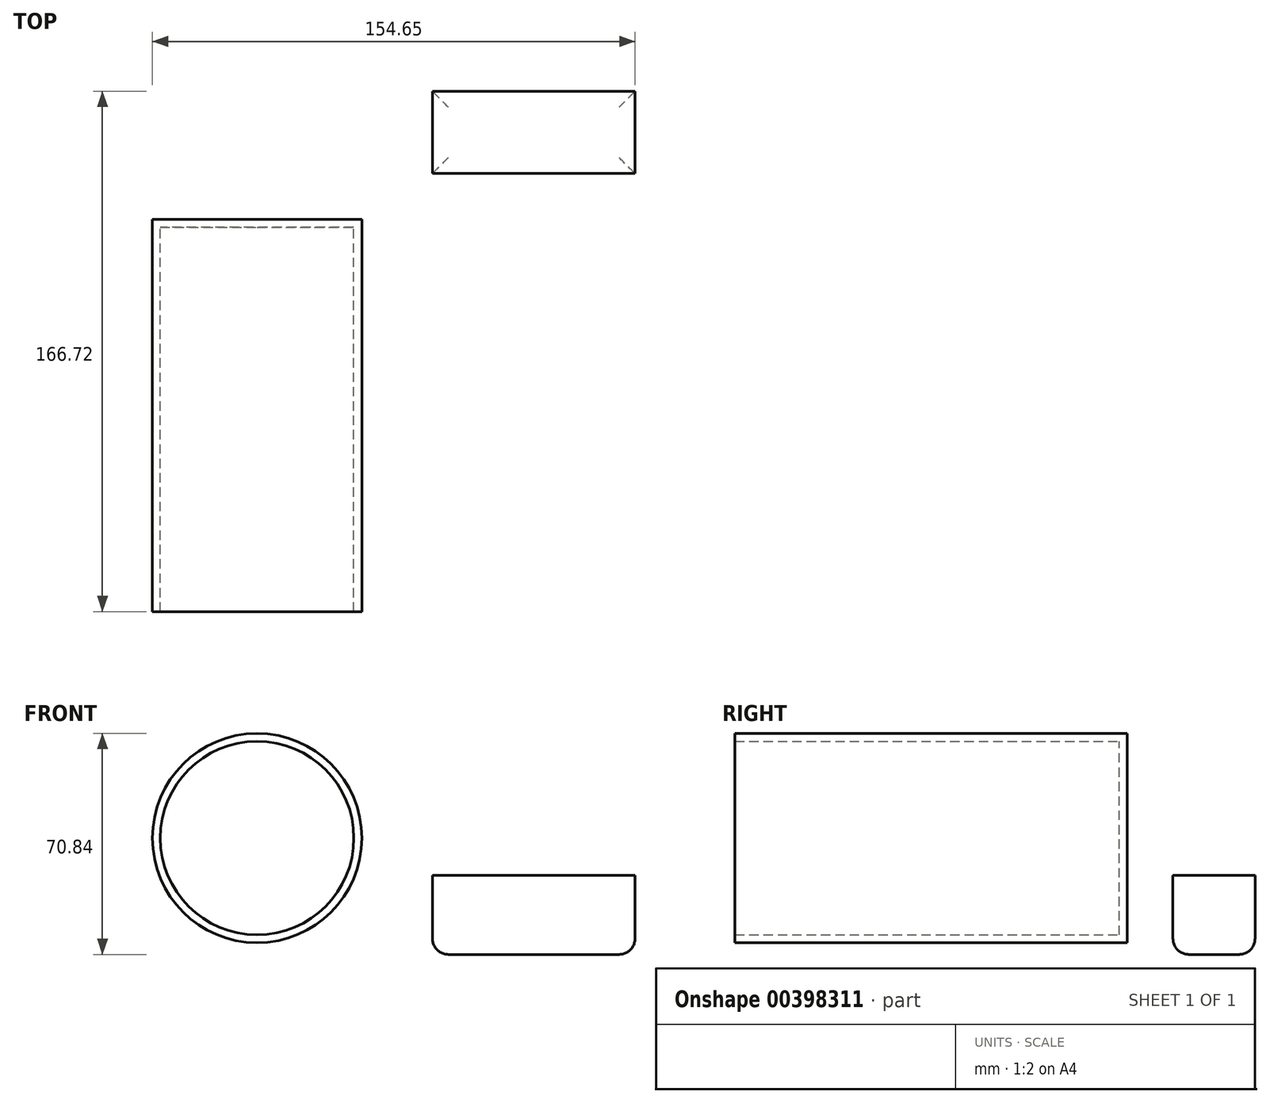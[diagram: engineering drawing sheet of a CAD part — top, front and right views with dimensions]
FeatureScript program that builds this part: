
annotation { "Feature Type Name" : "Feature", "Feature Type Description" : "" }
export const myFeature = defineFeature(function(context is Context, id is Id, definition is map)
    precondition{}
    {
        {
            var Q0;
            Q0=qCreatedBy(makeId("Front.planeOp"),FACE);
            var sketch = newSketch(context, id + "F0", { "sketchPlane" : qUnion([Q0])});
            skCircle(sketch, "E0", {"center": v(-48.38, 37.3) * mm, "radius": 33.55 * mm});
            skSolve(sketch);
        }
        {
            var Q0;
            Q0 = qSketchRegion(id + "F0", true);
            extrude(context, id + "F1", {"entities" : qUnion([Q0]), "depth" : 125.73 * mm});
        }
        {
            var Q0;
            Q0=makeQuery(id+"F1.opExtrude","CAP_FACE",FACE,{"disambiguationData":[OSD([sQuery(id+"F0.wireOp",EDGE,"E0")])],"isStart":false});
            shell(context, id + "F2", {"entities" : qUnion([Q0]), "thickness" : 2.54 * mm});
        }
        {
            var Q0;
            Q0=qCreatedBy(makeId("Top.planeOp"),FACE);
            var sketch = newSketch(context, id + "F3", { "sketchPlane" : qUnion([Q0])});
            skLineSegment(sketch, "E1.bottom", {"start": v(7.83, 40.99) * mm, "end": v(72.73, 40.99) * mm});
            skLineSegment(sketch, "E1.top", {"start": v(7.83, 14.67) * mm, "end": v(72.73, 14.67) * mm});
            skLineSegment(sketch, "E1.left", {"start": v(7.83, 40.99) * mm, "end": v(7.83, 14.67) * mm});
            skLineSegment(sketch, "E1.right", {"start": v(72.73, 40.99) * mm, "end": v(72.73, 14.67) * mm});
            skSolve(sketch);
        }
        {
            var Q0;
            Q0=makeQuery(id+"F3.imprint","IMPRINT",FACE,{"disambiguationData":[TD([[makeQuery(id+"F3.imprint","IMPRINT",EDGE,{"derivedFrom":sQuery(id+"F3.wireOp",EDGE,"E1.bottom")}),-1.0]])]});
            extrude(context, id + "F4", {"entities" : qUnion([Q0]), "depth" : 25.4 * mm});
        }
        {
            var Q0;
            Q0=makeQuery(id+"F4.opExtrude","CAP_FACE",FACE,{"disambiguationData":[OSD([sQuery(id+"F3.wireOp",EDGE,"E1.bottom"),sQuery(id+"F3.wireOp",EDGE,"E1.top"),sQuery(id+"F3.wireOp",EDGE,"E1.left"),sQuery(id+"F3.wireOp",EDGE,"E1.right")])],"isStart":true});
            fillet(context, id + "F5", {"entities" : qUnion([Q0]), "radius" : 5.08 * mm, "tangentPropagation" : true, "allowEdgeOverflow" : false});
        }
    });
